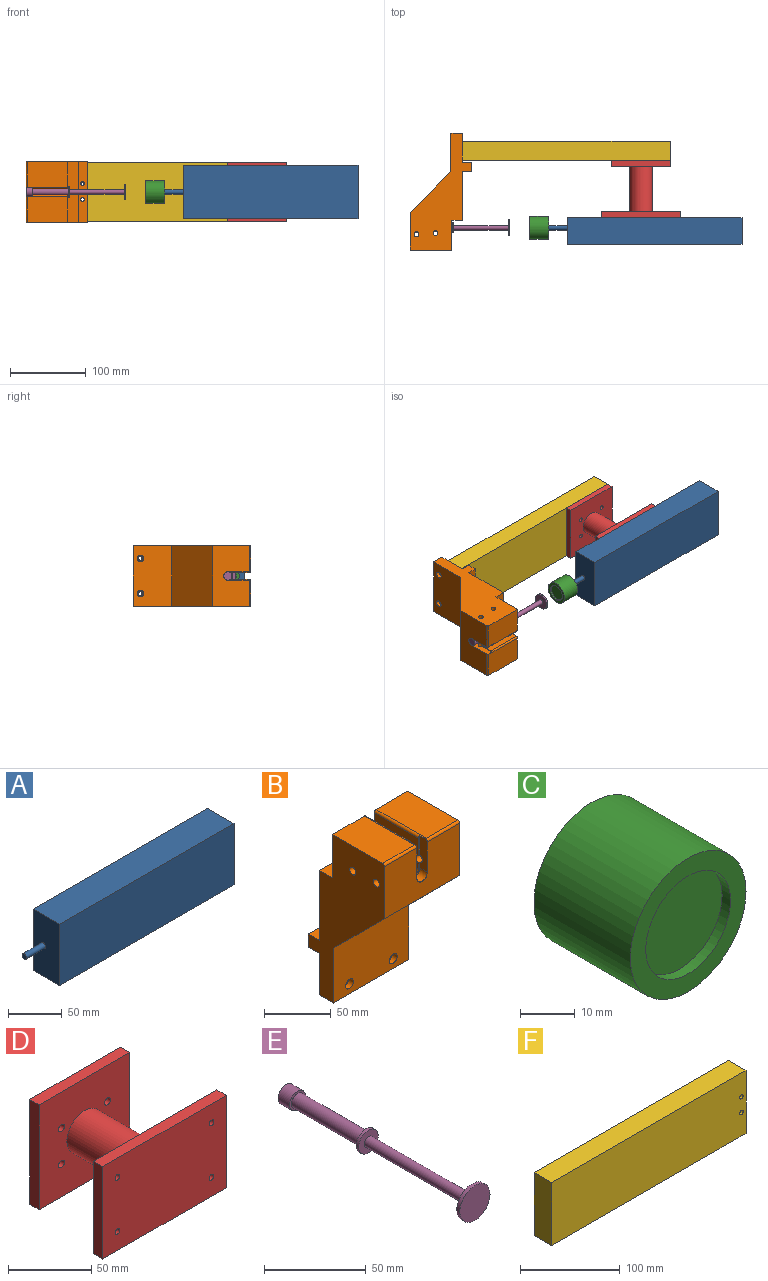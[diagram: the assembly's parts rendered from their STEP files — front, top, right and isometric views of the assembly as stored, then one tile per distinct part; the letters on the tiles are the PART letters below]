
ASSEMBLY  parts=6 mates=7
PART A: 8 faces, bbox 255x35x70 mm
  f0: plane 70x35mm, normal (1,0,0), area 2450mm2, adj f1,f3,f4,f5
  f1: plane 230x35mm, normal (0,0,1), area 8050mm2, adj f0,f2,f4,f5
  f2: plane 70x35mm, normal (-1,0,0), area 2421.7mm2, adj f1,f3,f4,f5,f6
  f3: plane 230x35mm, normal (0,0,-1), area 8050mm2, adj f0,f2,f4,f5
  f4: plane 230x70mm, normal (0,-1,0), area 16100mm2, adj f0,f1,f2,f3
  f5: plane 230x70mm, normal (0,1,0), area 16100mm2, adj f0,f1,f2,f3
  f6: cylinder r=3mm len=25mm, axis (1,0,0), area 471.2mm2, adj f2,f7
  f7: plane 6x6mm, normal (-1,0,0), area 28.3mm2, adj f6
PART B: 40 faces, bbox 80x81x154.5 mm
  f0: plane 53.18x33.83mm, normal (0,0,1), area 1798.9mm2, adj f3,f7,f36,f38
  f1: plane 80x64.5mm, normal (0,1,0), area 5160mm2, adj f3,f13,f14,f39
  f2: plane 53.18x33.83mm, normal (0,0,1), area 1798.9mm2, adj f8,f14,f37,f38
  f3: plane 154.5x81mm, normal (-1,0,0), area 5999.6mm2, adj f0,f1,f9,f13,f15,f16,f19,f20
  f4: plane 47.18x28mm, normal (1,0,0), area 1267.4mm2, adj f5,f7,f10,f12,f33,f34,f38
  f5: cylinder r=4.17mm len=47.18mm, axis (0,-1,0), area 618.9mm2, adj f4,f6,f10,f38
  f6: plane 47.18x28mm, normal (-1,0,0), area 1267.4mm2, adj f5,f8,f10,f11,f31,f32,f38
  f7: cylinder r=2mm len=53.81mm, axis (0,-1,0), area 152.2mm2, adj f0,f4,f12,f28,f36,f38
  f8: cylinder r=2mm len=53.81mm, axis (0,1,0), area 152.2mm2, adj f2,f6,f11,f30,f37,f38
  f9: plane 80x50.5mm, normal (0,-1,0), area 3926.5mm2, adj f3,f14,f15,f23,f25,f35
  f10: plane 11.1x10.86mm, normal (0,-1,0), area 35.6mm2, adj f4,f5,f6,f28,f29,f30,f32,f34
  f11: plane 18.21x1.38mm, normal (0,-1,0), area 24.3mm2, adj f6,f8,f30,f32
  f12: plane 18.21x1.38mm, normal (0,-1,0), area 24.3mm2, adj f4,f7,f28,f34
  f13: plane 80x12mm, normal (0,0,1), area 920.7mm2, adj f1,f3,f14,f20,f21,f22
  f14: plane 154.5x81mm, normal (1,0,0), area 5999.6mm2, adj f1,f2,f9,f13,f15,f16,f19,f20
  f15: plane 80x15mm, normal (0,0,-1), area 1200mm2, adj f3,f9,f14,f16
  f16: plane 80x38mm, normal (0,1,0), area 3000.7mm2, adj f3,f14,f15,f17,f18,f19
  f17: cylinder r=2.5mm len=10mm, axis (0,-1,0), area 157.1mm2, adj f16,f26
  f18: cylinder r=2.5mm len=10mm, axis (0,-1,0), area 157.1mm2, adj f16,f24
  f19: plane 80x12mm, normal (0,0,-1), area 920.7mm2, adj f3,f14,f16,f20,f21,f22
  f20: plane 80x12mm, normal (0,1,0), area 960mm2, adj f3,f13,f14,f19
  f21: cylinder r=2.5mm len=12mm, axis (0,0,1), area 188.5mm2, adj f13,f19
  f22: cylinder r=2.5mm len=12mm, axis (0,0,1), area 188.5mm2, adj f13,f19
  f23: cylinder r=4.25mm len=8.5mm, axis (0,-1,0), area 133.5mm2, adj f9,f24
  f24: plane 8.5x8.5mm, normal (0,-1,0), area 37.1mm2, adj f18,f23
  f25: cylinder r=4.25mm len=8.5mm, axis (0,-1,0), area 133.5mm2, adj f9,f26
  f26: plane 8.5x8.5mm, normal (0,-1,0), area 37.1mm2, adj f17,f25
  f27: plane 80x48mm, normal (0,-1,0), area 3480.8mm2, adj f3,f14,f28,f29,f30,f35,f36,f37
  f28: plane 29.9x8mm, normal (1,0,0), area 225.8mm2, adj f7,f10,f12,f27,f29,f34,f36
  f29: cylinder r=5.55mm len=11.1mm, axis (0,-1,0), area 139.5mm2, adj f10,f27,f28,f30
  f30: plane 29.9x8mm, normal (-1,0,0), area 225.8mm2, adj f8,f10,f11,f27,f29,f32,f37
  f31: cylinder r=3.25mm len=35.83mm, axis (1,0,0), area 731.6mm2, adj f6,f14
  f32: cylinder r=3.25mm len=35.83mm, axis (1,0,0), area 719.2mm2, adj f6,f10,f11,f14,f30
  f33: cylinder r=3.25mm len=35.83mm, axis (1,0,0), area 731.6mm2, adj f3,f4
  f34: cylinder r=3.25mm len=35.83mm, axis (1,0,0), area 719.2mm2, adj f3,f4,f10,f12,f28
  f35: plane 80x54mm, normal (0,-0.71,-0.71), area 6109.4mm2, adj f3,f9,f14,f27
  f36: cylinder r=2mm len=34.45mm, axis (1,0,0), area 108mm2, adj f0,f3,f7,f27,f28
  f37: cylinder r=2mm len=34.45mm, axis (1,0,0), area 108mm2, adj f2,f8,f14,f27,f30
  f38: plane 80x40mm, normal (0,1,0), area 2920.4mm2, adj f0,f2,f3,f4,f5,f6,f7,f8
  f39: plane 80x13.82mm, normal (0,0,1), area 1105.4mm2, adj f1,f3,f14,f38
PART C: 7 faces, bbox 30x25x30 mm
  f0: cylinder r=15mm len=30mm, axis (0,1,0), area 2356.2mm2, adj f1,f2
  f1: plane 30x30mm, normal (0,-1,0), area 326.7mm2, adj f0,f3
  f2: plane 30x30mm, normal (0,1,0), area 678.6mm2, adj f0,f5
  f3: cylinder r=11mm len=22mm, axis (0,-1,0), area 152.1mm2, adj f1,f4
  f4: plane 22x22mm, normal (0,-1,0), area 380.1mm2, adj f3
  f5: cylinder r=3mm len=9mm, axis (0,1,0), area 169.6mm2, adj f2,f6
  f6: plane 6x6mm, normal (0,1,0), area 28.3mm2, adj f5
PART D: 21 faces, bbox 105x76x77.2 mm
  f0: plane 68x8mm, normal (1,0,0), area 544mm2, adj f1,f7,f8,f9
  f1: plane 105x8mm, normal (0,0,1), area 840mm2, adj f0,f2,f8,f9
  f2: plane 68x8mm, normal (-1,0,0), area 544mm2, adj f1,f7,f8,f9
  f3: cylinder r=2mm len=8mm, axis (0,1,0), area 100.5mm2, adj f8,f9
  f4: cylinder r=2mm len=8mm, axis (0,1,0), area 100.5mm2, adj f8,f9
  f5: cylinder r=2mm len=8mm, axis (0,1,0), area 100.5mm2, adj f8,f9
  f6: cylinder r=2mm len=8mm, axis (0,1,0), area 100.5mm2, adj f8,f9
  f7: plane 105x8mm, normal (0,0,-1), area 840mm2, adj f0,f2,f8,f9
  f8: plane 105x68mm, normal (0,-1,0), area 7089.7mm2, adj f0,f1,f2,f3,f4,f5,f6,f7
  f9: plane 105x68mm, normal (0,1,0), area 6382.9mm2, adj f0,f1,f2,f3,f4,f5,f6,f7
  f10: cylinder r=15mm len=60mm, axis (0,-1,0), area 5654.9mm2, adj f9,f16
  f11: plane 77.2x8mm, normal (-1,0,0), area 617.6mm2, adj f12,f14,f15,f16
  f12: plane 77.2x8mm, normal (0,0,1), area 617.6mm2, adj f11,f13,f15,f16
  f13: plane 77.2x8mm, normal (1,0,0), area 617.6mm2, adj f12,f14,f15,f16
  f14: plane 77.2x8mm, normal (0,0,-1), area 617.6mm2, adj f11,f13,f15,f16
  f15: plane 77.2x77.2mm, normal (0,1,0), area 5881.3mm2, adj f11,f12,f13,f14,f17,f18,f19,f20
  f16: plane 77.2x77.2mm, normal (0,-1,0), area 5174.4mm2, adj f10,f11,f12,f13,f14,f17,f18,f19
  f17: cylinder r=2.5mm len=8mm, axis (0,1,0), area 125.7mm2, adj f15,f16
  f18: cylinder r=2.5mm len=8mm, axis (0,1,0), area 125.7mm2, adj f15,f16
  f19: cylinder r=2.5mm len=8mm, axis (0,1,0), area 125.7mm2, adj f15,f16
  f20: cylinder r=2.5mm len=8mm, axis (0,1,0), area 125.7mm2, adj f15,f16
PART E: 11 faces, bbox 21x131.6x21 mm
  f0: cylinder r=5.55mm len=11.1mm, axis (0,1,0), area 279mm2, adj f1,f2
  f1: plane 11.1x11.1mm, normal (0,-1,0), area 42mm2, adj f0,f3
  f2: plane 11.1x11.1mm, normal (0,1,0), area 96.8mm2, adj f0
  f3: cylinder r=4.17mm len=47.7mm, axis (0,1,0), area 1251.3mm2, adj f1,f6
  f4: cylinder r=6.8mm len=13.6mm, axis (0,1,0), area 76.9mm2, adj f5,f6
  f5: plane 13.6x13.6mm, normal (0,-1,0), area 117mm2, adj f4,f7
  f6: plane 13.6x13.6mm, normal (0,1,0), area 90.5mm2, adj f3,f4
  f7: cylinder r=3mm len=72mm, axis (0,1,0), area 1357.2mm2, adj f5,f10
  f8: cylinder r=10.5mm len=21mm, axis (0,1,0), area 138.5mm2, adj f9,f10
  f9: plane 21x21mm, normal (0,-1,0), area 346.4mm2, adj f8
  f10: plane 21x21mm, normal (0,1,0), area 318.1mm2, adj f7,f8
PART F: 8 faces, bbox 275x25x77.2 mm
  f0: plane 77.2x25mm, normal (1,0,0), area 1930mm2, adj f1,f3,f4,f5
  f1: plane 275x25mm, normal (0,0,1), area 6875mm2, adj f0,f2,f4,f5
  f2: plane 77.2x25mm, normal (-1,0,0), area 1930mm2, adj f1,f3,f4,f5
  f3: plane 275x25mm, normal (0,0,-1), area 6875mm2, adj f0,f2,f4,f5
  f4: plane 275x77.2mm, normal (0,-1,0), area 21190.7mm2, adj f0,f1,f2,f3,f6,f7
  f5: plane 275x77.2mm, normal (0,1,0), area 21190.7mm2, adj f0,f1,f2,f3,f6,f7
  f6: cylinder r=2.5mm len=25mm, axis (0,-1,0), area 392.7mm2, adj f4,f5
  f7: cylinder r=2.5mm len=25mm, axis (0,-1,0), area 392.7mm2, adj f4,f5
PLACE A t=(142.63,45.91,42.5)mm
PLACE B rot(axis=(0.58,0.58,-0.58),120deg) t=(-111.07,132.08,42.5)mm
PLACE C rot(axis=(0,0,-1),90deg) t=(2.63,32.58,42.5)mm
PLACE D rot(axis=(0,-1,0),180deg) t=(124.33,53.91,42.41)mm
PLACE E rot(axis=(0,0,1),90deg) t=(-180.07,32.58,42.5)mm
PLACE F rot(axis=(0,-1,0),180deg) t=(33.38,146.91,42.41)mm
MATE planar F.f2 <-> D.f11  axis (1,0,0) through (162.93,121.91,81.01)mm
MATE cylindrical C.f0 <-> A.f6  axis (1,0,0) through (2.63,32.58,42.5)mm
MATE planar D.f10 <-> A.f5  axis (0,-1,0) through (124.33,45.91,42.41)mm
MATE cylindrical B.f21 <-> F.f7  axis (0,-1,0) through (-105.57,107.08,32.81)mm
MATE cylindrical E.f0 <-> B.f29  axis (-1,0,0) through (-180.07,32.58,42.5)mm
MATE planar D.f18 <-> F.f4  axis (0,1,0) through (104.73,121.91,56.81)mm
MATE planar D.f14 <-> F.f3  axis (0,0,1) through (124.33,117.91,81.01)mm
